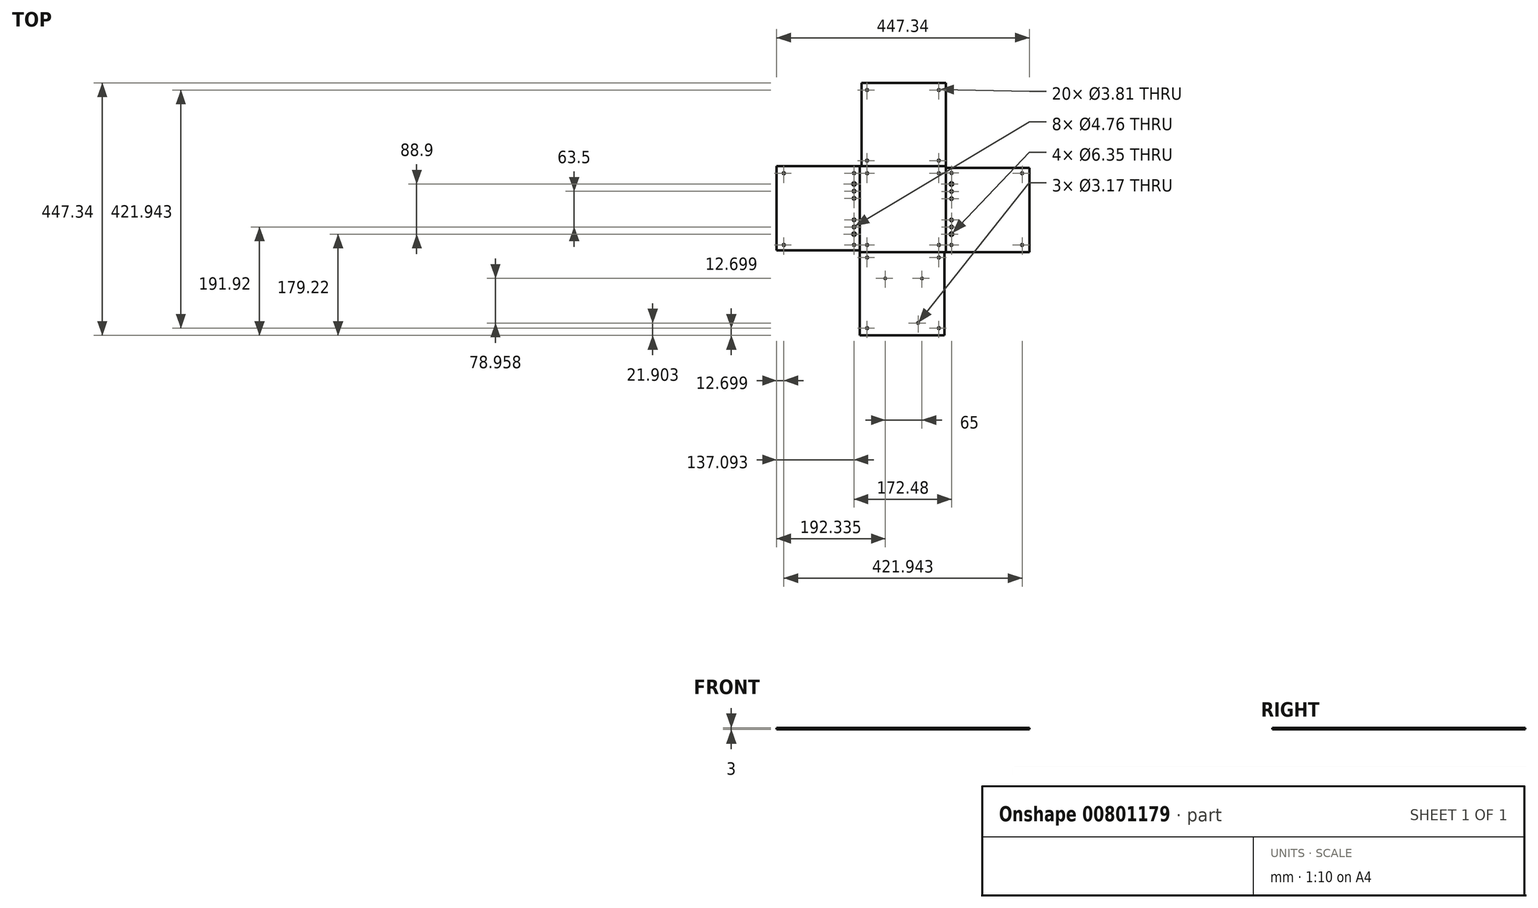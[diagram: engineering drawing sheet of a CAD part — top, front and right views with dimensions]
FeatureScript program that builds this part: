
annotation { "Feature Type Name" : "Feature", "Feature Type Description" : "" }
export const myFeature = defineFeature(function(context is Context, id is Id, definition is map)
    precondition{}
    {
        {
            var Q0;
            Q0=qCreatedBy(makeId("Top.planeOp"),FACE);
            var sketch = newSketch(context, id + "F0", { "sketchPlane" : qUnion([Q0])});
            skLineSegment(sketch, "E0.bottom", {"start": v(0, 0) * mm, "end": v(152.4, 0) * mm});
            skLineSegment(sketch, "E0.top", {"start": v(0, 152.4) * mm, "end": v(152.4, 152.4) * mm});
            skLineSegment(sketch, "E0.left", {"start": v(0, 0) * mm, "end": v(0, 152.4) * mm});
            skLineSegment(sketch, "E0.right", {"start": v(152.4, 0) * mm, "end": v(152.4, 152.4) * mm});
            skLineSegment(sketch, "E1.bottom", {"start": v(0, 152.4) * mm, "end": v(-147.47, 152.4) * mm});
            skLineSegment(sketch, "E1.top", {"start": v(0, 3) * mm, "end": v(-147.47, 3) * mm});
            skLineSegment(sketch, "E1.left", {"start": v(0, 152.4) * mm, "end": v(0, 3) * mm});
            skLineSegment(sketch, "E1.right", {"start": v(-147.47, 152.4) * mm, "end": v(-147.47, 3) * mm});
            skLineSegment(sketch, "E2.bottom", {"start": v(0, 0) * mm, "end": v(149.4, 0) * mm});
            skLineSegment(sketch, "E2.top", {"start": v(0, -147.47) * mm, "end": v(149.4, -147.47) * mm});
            skLineSegment(sketch, "E2.left", {"start": v(0, 0) * mm, "end": v(0, -147.47) * mm});
            skLineSegment(sketch, "E2.right", {"start": v(149.4, 0) * mm, "end": v(149.4, -147.47) * mm});
            skLineSegment(sketch, "E3.bottom", {"start": v(152.4, 0) * mm, "end": v(299.87, 0) * mm});
            skLineSegment(sketch, "E3.top", {"start": v(152.4, 149.4) * mm, "end": v(299.87, 149.4) * mm});
            skLineSegment(sketch, "E3.left", {"start": v(152.4, 0) * mm, "end": v(152.4, 149.4) * mm});
            skLineSegment(sketch, "E3.right", {"start": v(299.87, 0) * mm, "end": v(299.87, 149.4) * mm});
            skLineSegment(sketch, "E4.bottom", {"start": v(152.4, 152.4) * mm, "end": v(3, 152.4) * mm});
            skLineSegment(sketch, "E4.top", {"start": v(152.4, 299.87) * mm, "end": v(3, 299.87) * mm});
            skLineSegment(sketch, "E4.left", {"start": v(152.4, 152.4) * mm, "end": v(152.4, 299.87) * mm});
            skLineSegment(sketch, "E4.right", {"start": v(3, 152.4) * mm, "end": v(3, 299.87) * mm});
            skLineSegment(sketch, "E5", {"start": v(152.4, 149.4) * mm, "end": v(152.4, 0) * mm});
            skCircle(sketch, "E6", {"center": v(-10.38, 120.65) * mm, "radius": 3.18 * mm});
            skCircle(sketch, "E7", {"center": v(-10.38, 107.95) * mm, "radius": 2.38 * mm});
            skCircle(sketch, "E8", {"center": v(-10.38, 95.25) * mm, "radius": 2.38 * mm});
            skCircle(sketch, "E9.MirrorC", {"center": v(-10.38, 31.75) * mm, "radius": 3.18 * mm});
            skCircle(sketch, "E10.MirrorC", {"center": v(-10.38, 44.45) * mm, "radius": 2.38 * mm});
            skCircle(sketch, "E11.MirrorC", {"center": v(-10.38, 57.15) * mm, "radius": 2.38 * mm});
            skCircle(sketch, "E12.MirrorC", {"center": v(162.1, 107.43) * mm, "radius": 2.38 * mm});
            skCircle(sketch, "E13.MirrorC", {"center": v(162.1, 120.65) * mm, "radius": 3.18 * mm});
            skCircle(sketch, "E14.MirrorC", {"center": v(162.1, 94.7) * mm, "radius": 2.38 * mm});
            skCircle(sketch, "E15.MirrorC", {"center": v(162.1, 56.97) * mm, "radius": 2.38 * mm});
            skCircle(sketch, "E16.MirrorC", {"center": v(162.1, 44.57) * mm, "radius": 2.38 * mm});
            skCircle(sketch, "E17.MirrorC", {"center": v(162.1, 31.75) * mm, "radius": 3.18 * mm});
            skCircle(sketch, "E18", {"center": v(-10.38, 139.7) * mm, "radius": 1.9 * mm});
            skCircle(sketch, "E19", {"center": v(-134.77, 139.7) * mm, "radius": 1.9 * mm});
            skCircle(sketch, "E20", {"center": v(-134.77, 12.7) * mm, "radius": 1.9 * mm});
            skCircle(sketch, "E21", {"center": v(-10.38, 12.7) * mm, "radius": 1.9 * mm});
            skCircle(sketch, "E22.MirrorC", {"center": v(162.1, 12.7) * mm, "radius": 1.9 * mm});
            skCircle(sketch, "E23.MirrorC", {"center": v(287.17, 12.7) * mm, "radius": 1.9 * mm});
            skCircle(sketch, "E24.MirrorC", {"center": v(287.17, 139.7) * mm, "radius": 1.9 * mm});
            skCircle(sketch, "E25.MirrorC", {"center": v(162.1, 140.05) * mm, "radius": 1.9 * mm});
            skCircle(sketch, "E26", {"center": v(139.7, 287.17) * mm, "radius": 1.9 * mm});
            skCircle(sketch, "E27", {"center": v(139.7, 162.1) * mm, "radius": 1.9 * mm});
            skCircle(sketch, "E28", {"center": v(12.7, 162.1) * mm, "radius": 1.9 * mm});
            skCircle(sketch, "E29", {"center": v(12.7, 287.17) * mm, "radius": 1.9 * mm});
            skCircle(sketch, "E30", {"center": v(12.7, -9.7) * mm, "radius": 1.9 * mm});
            skCircle(sketch, "E31", {"center": v(139.7, -9.7) * mm, "radius": 1.9 * mm});
            skCircle(sketch, "E32", {"center": v(139.7, -134.77) * mm, "radius": 1.9 * mm});
            skCircle(sketch, "E33", {"center": v(12.7, -134.77) * mm, "radius": 1.9 * mm});
            skCircle(sketch, "E34", {"center": v(12.7, 139.7) * mm, "radius": 1.9 * mm});
            skCircle(sketch, "E35", {"center": v(139.7, 139.7) * mm, "radius": 1.9 * mm});
            skCircle(sketch, "E36", {"center": v(12.7, 12.7) * mm, "radius": 1.9 * mm});
            skCircle(sketch, "E37", {"center": v(139.7, 12.7) * mm, "radius": 1.9 * mm});
            skPoint(sketch, "E38", {"position": v(77.7, 152.4) * mm});
            skPoint(sketch, "E39", {"position": v(152.4, 74.7) * mm});
            skLineSegment(sketch, "E40.bottom", {"start": v(32.82, -131.65) * mm, "end": v(32.82, -41.4) * mm});
            skLineSegment(sketch, "E40.top", {"start": v(117.62, -131.65) * mm, "end": v(117.62, -41.4) * mm});
            skLineSegment(sketch, "E40.left", {"start": v(32.82, -131.65) * mm, "end": v(117.62, -131.65) * mm});
            skLineSegment(sketch, "E40.right", {"start": v(32.82, -41.4) * mm, "end": v(117.62, -41.4) * mm});
            skPoint(sketch, "E41", {"position": v(32.82, -86.53) * mm});
            skCircle(sketch, "E42", {"center": v(44.86, -46.6) * mm, "radius": 1.59 * mm});
            skCircle(sketch, "E43", {"center": v(109.86, -46.6) * mm, "radius": 1.59 * mm});
            skPoint(sketch, "E44", {"position": v(75.22, -41.4) * mm});
            skCircle(sketch, "E45", {"center": v(102.97, -125.57) * mm, "radius": 1.59 * mm});
            skSolve(sketch);
        }
        {
            var Q0;
            Q0=makeQuery(id+"F0.imprint","IMPRINT",FACE,{"disambiguationData":[TD([[makeQuery(id+"F0.imprint","IMPRINT",EDGE,{"derivedFrom":sQuery(id+"F0.wireOp",EDGE,"E34")}),-1.0]])]});
            var Q1;
            Q1=makeQuery(id+"F0.imprint","IMPRINT",FACE,{"disambiguationData":[TD([[makeQuery(id+"F0.imprint","IMPRINT",EDGE,{"derivedFrom":sQuery(id+"F0.wireOp",EDGE,"1b204d8b-61c5-4b83-bd07-62cc8ea12c2b.bottom")}),-1.0]])]});
            extrude(context, id + "F1", {"entities" : qUnion([Q0, Q1]), "depth" : 3 * mm, "offsetDistance" : 25.4 * mm});
        }
        {
            var Q0;
            Q0=makeQuery(id+"F0.imprint","IMPRINT",FACE,{"disambiguationData":[TD([[makeQuery(id+"F0.imprint","IMPRINT",EDGE,{"derivedFrom":sQuery(id+"F0.wireOp",EDGE,"E4.top")}),1.0]])]});
            extrude(context, id + "F2", {"entities" : qUnion([Q0]), "depth" : 3 * mm, "offsetDistance" : 25.4 * mm});
        }
        {
            var Q0;
            {var subQ2=sQuery(id+"F0.wireOp",EDGE,"E1.bottom");Q0=makeQuery(id+"F0.imprint","IMPRINT",FACE,{"disambiguationData":[TD([[makeQuery(id+"F0.imprint","IMPRINT",EDGE,{"derivedFrom":subQ2}),1.0]])]});}
            extrude(context, id + "F3", {"entities" : qUnion([Q0]), "depth" : 3 * mm, "offsetDistance" : 25.4 * mm});
        }
        {
            var Q0;
            Q0=makeQuery(id+"F0.imprint","IMPRINT",FACE,{"disambiguationData":[TD([[makeQuery(id+"F0.imprint","IMPRINT",EDGE,{"derivedFrom":sQuery(id+"F0.wireOp",EDGE,"E2.top")}),1.0]])]});
            extrude(context, id + "F4", {"entities" : qUnion([Q0]), "depth" : 3 * mm, "offsetDistance" : 25.4 * mm});
        }
        {
            var Q0;
            {var subQ0=sQuery(id+"F0.wireOp",EDGE,"E3.bottom");Q0=makeQuery(id+"F0.imprint","IMPRINT",FACE,{"disambiguationData":[TD([[makeQuery(id+"F0.imprint","IMPRINT",EDGE,{"derivedFrom":subQ0}),1.0]])]});}
            extrude(context, id + "F5", {"entities" : qUnion([Q0]), "depth" : 3 * mm, "offsetDistance" : 25.4 * mm});
        }
        {
            var Q0;
            Q0=makeQuery(id+"F0.imprint","IMPRINT",FACE,{"disambiguationData":[TD([[makeQuery(id+"F0.imprint","IMPRINT",EDGE,{"derivedFrom":sQuery(id+"F0.wireOp",EDGE,"E40.bottom")}),-1.0]])]});
            extrude(context, id + "F6", {"entities" : qUnion([Q0]), "operationType" : NewBodyOperationType.ADD, "depth" : 3 * mm, "offsetDistance" : 25.4 * mm});
        }
    });
